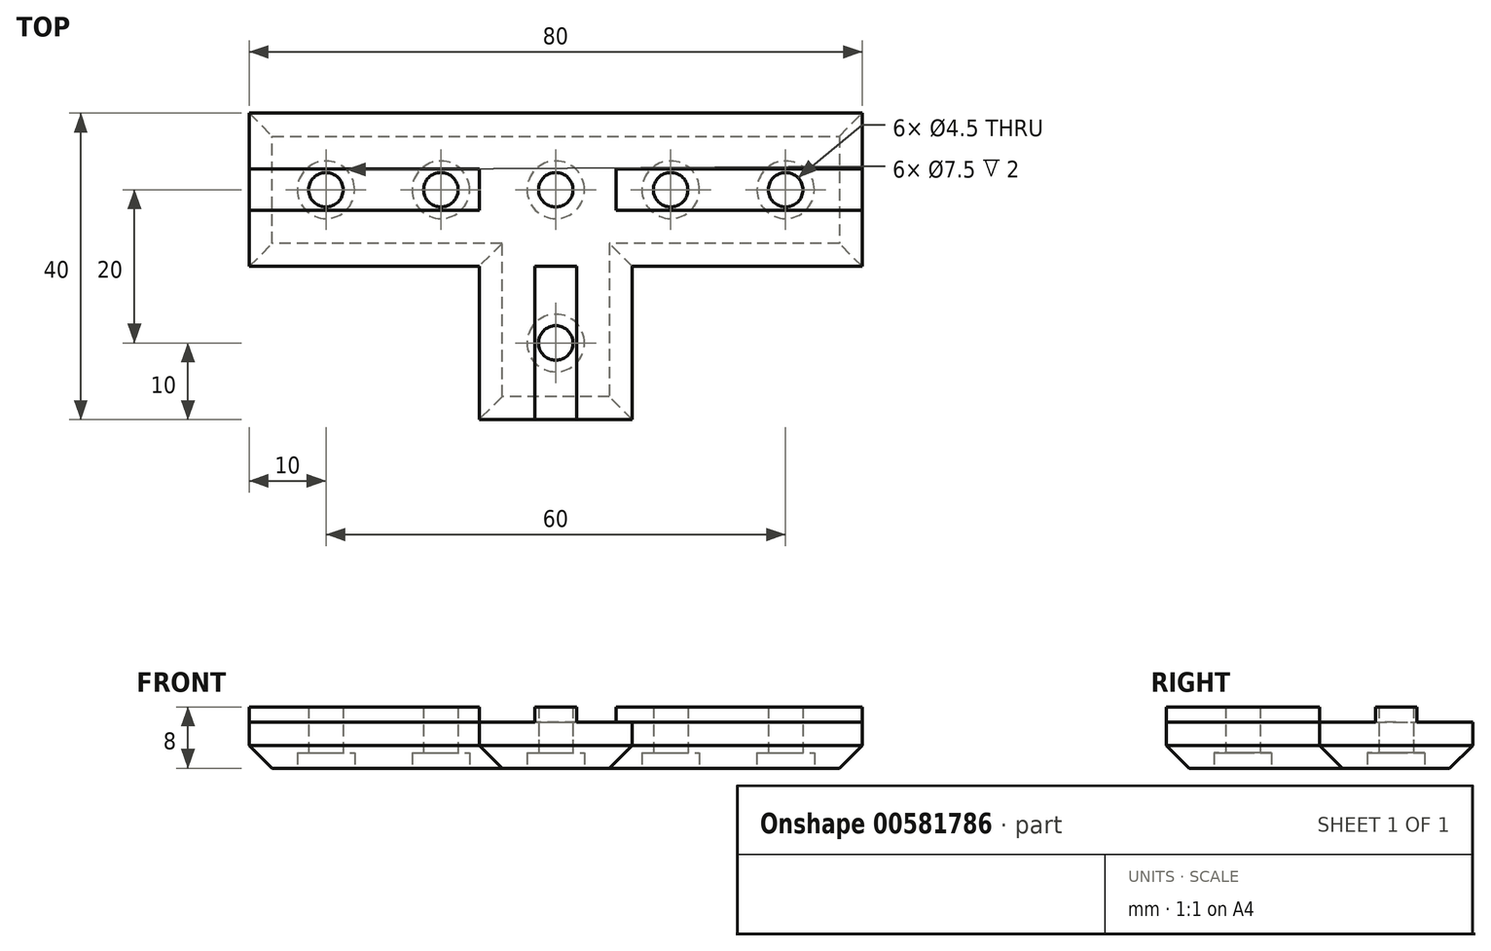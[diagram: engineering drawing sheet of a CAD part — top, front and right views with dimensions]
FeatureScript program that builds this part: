
annotation { "Feature Type Name" : "Feature", "Feature Type Description" : "" }
export const myFeature = defineFeature(function(context is Context, id is Id, definition is map)
    precondition{}
    {
        {
            var Q0;
            Q0=qCreatedBy(makeId("Top.planeOp"),FACE);
            var sketch = newSketch(context, id + "F0", { "sketchPlane" : qUnion([Q0])});
            skLineSegment(sketch, "E0", {"start": v(0, 0) * mm, "end": v(0, 20) * mm, "construction": true});
            skLineSegment(sketch, "E1", {"start": v(0, 0) * mm, "end": v(0, -20) * mm, "construction": true});
            skLineSegment(sketch, "E2", {"start": v(-10, 0) * mm, "end": v(-40, 0) * mm});
            skLineSegment(sketch, "E3", {"start": v(0, 20) * mm, "end": v(-40, 20) * mm});
            skLineSegment(sketch, "E4", {"start": v(-40, 20) * mm, "end": v(-40, 0) * mm});
            skLineSegment(sketch, "E5", {"start": v(0, 20) * mm, "end": v(40, 20) * mm});
            skLineSegment(sketch, "E6", {"start": v(40, 20) * mm, "end": v(40, 0) * mm});
            skLineSegment(sketch, "E7", {"start": v(40, 0) * mm, "end": v(10, 0) * mm});
            skLineSegment(sketch, "E8", {"start": v(0, -20) * mm, "end": v(10, -20) * mm});
            skLineSegment(sketch, "E9", {"start": v(10, -20) * mm, "end": v(10, 0) * mm});
            skLineSegment(sketch, "E10", {"start": v(0, -20) * mm, "end": v(-10, -20) * mm});
            skLineSegment(sketch, "E11", {"start": v(-10, -20) * mm, "end": v(-10, 0) * mm});
            skSolve(sketch);
        }
        {
            var Q0;
            Q0=qSketchRegion(id+"F0",true);
            extrude(context, id + "F1", {"entities" : qUnion([Q0]), "depth" : 6 * mm});
        }
        {
            var Q0;
            Q0=makeQuery(id+"F1.opExtrude","CAP_FACE",FACE,{"disambiguationData":[OSD([sQuery(id+"F0.wireOp",EDGE,"E2"),sQuery(id+"F0.wireOp",EDGE,"E3"),sQuery(id+"F0.wireOp",EDGE,"E4"),sQuery(id+"F0.wireOp",EDGE,"E5"),sQuery(id+"F0.wireOp",EDGE,"E6"),sQuery(id+"F0.wireOp",EDGE,"E7"),sQuery(id+"F0.wireOp",EDGE,"E8"),sQuery(id+"F0.wireOp",EDGE,"E9"),sQuery(id+"F0.wireOp",EDGE,"E10"),sQuery(id+"F0.wireOp",EDGE,"E11")])],"isStart":false});
            var sketch = newSketch(context, id + "F2", { "sketchPlane" : qUnion([Q0])});
            skLineSegment(sketch, "E12", {"start": v(-40, 10) * mm, "end": v(40, 10) * mm, "construction": true});
            skLineSegment(sketch, "E13", {"start": v(0, -20) * mm, "end": v(0, 0) * mm, "construction": true});
            skLineSegment(sketch, "E14", {"start": v(0, 0) * mm, "end": v(-2.71, 0) * mm});
            skLineSegment(sketch, "E15", {"start": v(-2.71, 0) * mm, "end": v(-2.7, -20) * mm});
            skLineSegment(sketch, "E16", {"start": v(2.71, -20) * mm, "end": v(2.71, 0) * mm});
            skLineSegment(sketch, "E17", {"start": v(2.71, 0) * mm, "end": v(0, 0) * mm});
            skLineSegment(sketch, "E18", {"start": v(-2.7, -20) * mm, "end": v(2.71, -20) * mm});
            skLineSegment(sketch, "E19", {"start": v(7.85, 10) * mm, "end": v(7.85, 12.71) * mm});
            skLineSegment(sketch, "E20", {"start": v(7.85, 12.71) * mm, "end": v(40, 12.71) * mm});
            skLineSegment(sketch, "E21", {"start": v(40, 12.7) * mm, "end": v(40, 7.3) * mm});
            skLineSegment(sketch, "E22", {"start": v(40, 7.3) * mm, "end": v(7.85, 7.29) * mm});
            skLineSegment(sketch, "E23", {"start": v(7.85, 7.29) * mm, "end": v(7.85, 10) * mm});
            skLineSegment(sketch, "E24", {"start": v(-40, 12.7) * mm, "end": v(-40, 7.29) * mm});
            skLineSegment(sketch, "E25", {"start": v(-40, 7.29) * mm, "end": v(-10, 7.29) * mm});
            skLineSegment(sketch, "E26", {"start": v(-10, 7.29) * mm, "end": v(-10, 12.71) * mm});
            skLineSegment(sketch, "E27", {"start": v(-10, 12.71) * mm, "end": v(-40, 12.71) * mm});
            skSolve(sketch);
        }
        {
            var Q0;
            Q0=qSketchRegion(id+"F2",true);
            extrude(context, id + "F3", {"entities" : qUnion([Q0]), "operationType" : NewBodyOperationType.ADD, "depth" : 2 * mm});
        }
        {
            var Q0;
            Q0=makeQuery(id+"F1.opExtrude","CAP_FACE",FACE,{"disambiguationData":[OSD([sQuery(id+"F0.wireOp",EDGE,"E2"),sQuery(id+"F0.wireOp",EDGE,"E3"),sQuery(id+"F0.wireOp",EDGE,"E4"),sQuery(id+"F0.wireOp",EDGE,"E5"),sQuery(id+"F0.wireOp",EDGE,"E6"),sQuery(id+"F0.wireOp",EDGE,"E7"),sQuery(id+"F0.wireOp",EDGE,"E8"),sQuery(id+"F0.wireOp",EDGE,"E9"),sQuery(id+"F0.wireOp",EDGE,"E10"),sQuery(id+"F0.wireOp",EDGE,"E11")])],"isStart":true});
            var sketch = newSketch(context, id + "F4", { "sketchPlane" : qUnion([Q0])});
            skCircle(sketch, "E28", {"center": v(-30, -10) * mm, "radius": 2.25 * mm});
            skCircle(sketch, "E29", {"center": v(0, -10) * mm, "radius": 2.25 * mm});
            skCircle(sketch, "E30", {"center": v(0, 10) * mm, "radius": 2.25 * mm});
            skCircle(sketch, "E31", {"center": v(30, -10) * mm, "radius": 2.25 * mm});
            skCircle(sketch, "E32", {"center": v(15, -10) * mm, "radius": 2.25 * mm});
            skCircle(sketch, "E33", {"center": v(-15, -10) * mm, "radius": 2.25 * mm});
            skSolve(sketch);
        }
        {
            var Q0;
            Q0=qSketchRegion(id+"F4",true);
            extrude(context, id + "F5", {"entities" : qUnion([Q0]), "operationType" : NewBodyOperationType.REMOVE, "endBound" : BoundingType.THROUGH_ALL, "oppositeDirection" : true, "depth" : 25 * mm});
        }
        {
            var Q0;
            Q0=makeQuery(id+"F1.opExtrude","CAP_FACE",FACE,{"disambiguationData":[OSD([sQuery(id+"F0.wireOp",EDGE,"E2"),sQuery(id+"F0.wireOp",EDGE,"E3"),sQuery(id+"F0.wireOp",EDGE,"E4"),sQuery(id+"F0.wireOp",EDGE,"E5"),sQuery(id+"F0.wireOp",EDGE,"E6"),sQuery(id+"F0.wireOp",EDGE,"E7"),sQuery(id+"F0.wireOp",EDGE,"E8"),sQuery(id+"F0.wireOp",EDGE,"E9"),sQuery(id+"F0.wireOp",EDGE,"E10"),sQuery(id+"F0.wireOp",EDGE,"E11")])],"isStart":true});
            var sketch = newSketch(context, id + "F6", { "sketchPlane" : qUnion([Q0])});
            skCircle(sketch, "E34", {"center": v(0, 10) * mm, "radius": 3.75 * mm});
            skCircle(sketch, "E35", {"center": v(0, -10) * mm, "radius": 3.75 * mm});
            skCircle(sketch, "E36", {"center": v(30, -10) * mm, "radius": 3.75 * mm});
            skCircle(sketch, "E37", {"center": v(-30, -10) * mm, "radius": 3.75 * mm});
            skCircle(sketch, "E38", {"center": v(-15, -10) * mm, "radius": 3.75 * mm});
            skCircle(sketch, "E39", {"center": v(15, -10) * mm, "radius": 3.75 * mm});
            skSolve(sketch);
        }
        {
            var Q0;
            Q0=qSketchRegion(id+"F6",true);
            extrude(context, id + "F7", {"entities" : qUnion([Q0]), "operationType" : NewBodyOperationType.REMOVE, "oppositeDirection" : true, "depth" : 2 * mm});
        }
        {
            var Q0;
            Q0=makeQuery(id+"F1.opExtrude","CAP_EDGE",EDGE,{"disambiguationData":[OSD([sQuery(id+"F0.wireOp",EDGE,"E11")])],"isStart":true});
            var Q1;
            Q1=makeQuery(id+"F1.opExtrude","CAP_EDGE",EDGE,{"disambiguationData":[OSD([sQuery(id+"F0.wireOp",EDGE,"E2")])],"isStart":true});
            var Q2;
            Q2=makeQuery(id+"F1.opExtrude","CAP_EDGE",EDGE,{"disambiguationData":[OSD([sQuery(id+"F0.wireOp",EDGE,"E9")])],"isStart":true});
            var Q3;
            Q3=makeQuery(id+"F1.opExtrude","CAP_EDGE",EDGE,{"disambiguationData":[OSD([sQuery(id+"F0.wireOp",EDGE,"E7")])],"isStart":true});
            var Q4;
            Q4=makeQuery(id+"F1.opExtrude","CAP_EDGE",EDGE,{"disambiguationData":[OSD([sQuery(id+"F0.wireOp",EDGE,"E3"),sQuery(id+"F0.wireOp",EDGE,"E5")])],"isStart":true});
            var Q5;
            Q5=makeQuery(id+"F1.opExtrude","CAP_EDGE",EDGE,{"disambiguationData":[OSD([sQuery(id+"F0.wireOp",EDGE,"E6")])],"isStart":true});
            var Q6;
            Q6=makeQuery(id+"F1.opExtrude","CAP_EDGE",EDGE,{"disambiguationData":[OSD([sQuery(id+"F0.wireOp",EDGE,"E4")])],"isStart":true});
            var Q7;
            Q7=makeQuery(id+"F1.opExtrude","CAP_EDGE",EDGE,{"disambiguationData":[OSD([sQuery(id+"F0.wireOp",EDGE,"E8"),sQuery(id+"F0.wireOp",EDGE,"E10")])],"isStart":true});
            chamfer(context, id + "F8", {"entities" : qUnion([Q0, Q1, Q2, Q3, Q4, Q5, Q6, Q7]), "width" : 3 * mm, "tangentPropagation" : true});
        }
    });
